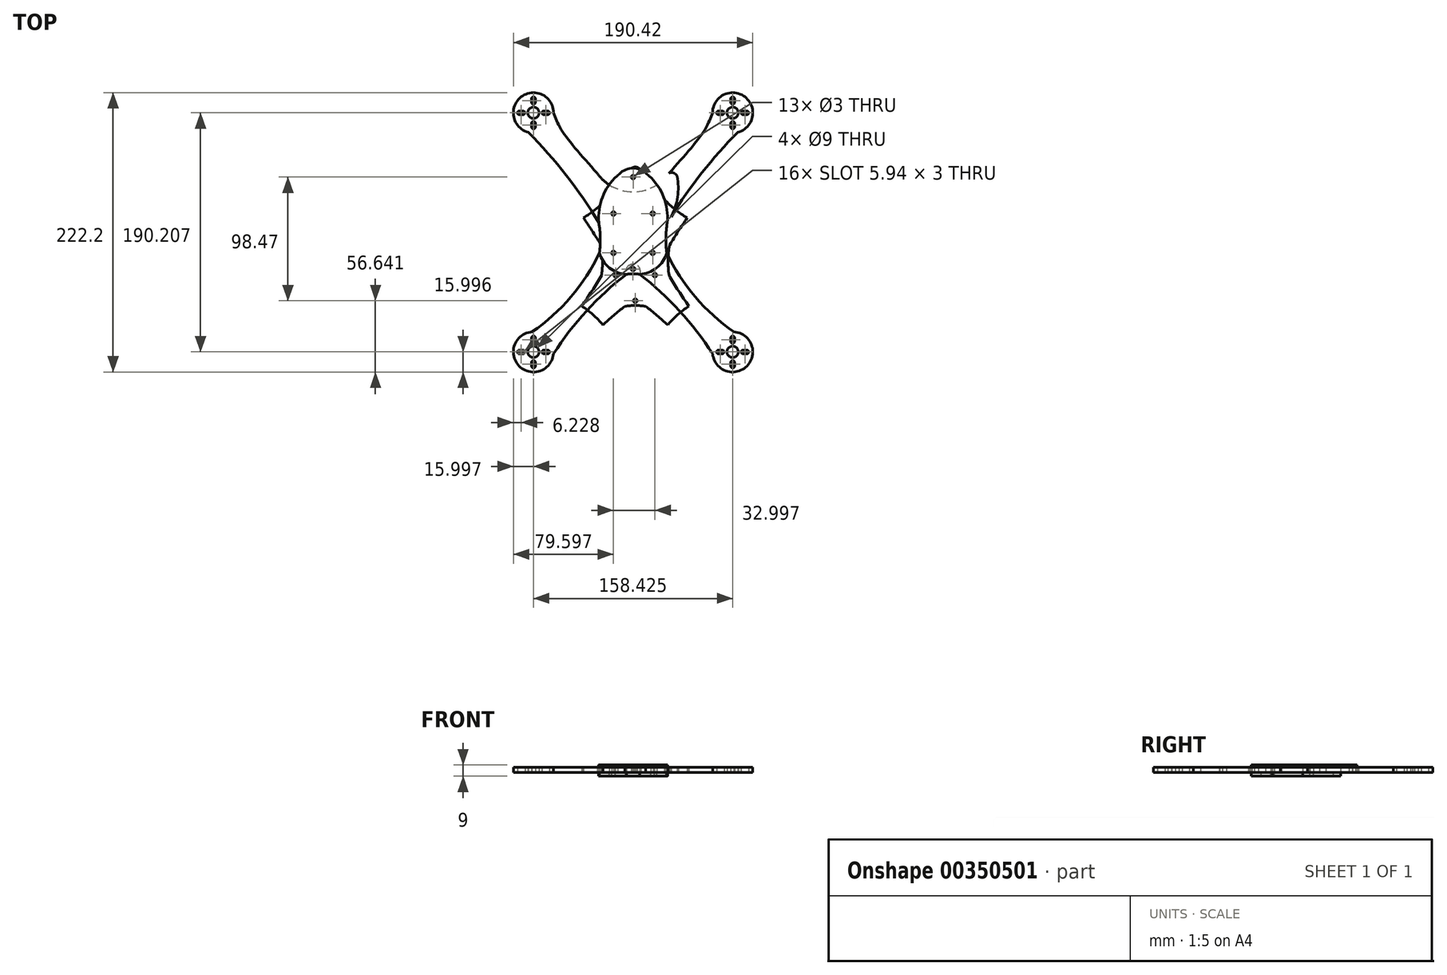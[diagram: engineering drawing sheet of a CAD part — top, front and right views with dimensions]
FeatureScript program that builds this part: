
annotation { "Feature Type Name" : "Feature", "Feature Type Description" : "" }
export const myFeature = defineFeature(function(context is Context, id is Id, definition is map)
    precondition{}
    {
        {
            var Q0;
            Q0=qCreatedBy(makeId("Top.planeOp"),FACE);
            var sketch = newSketch(context, id + "F0", { "sketchPlane" : qUnion([Q0])});
            skArc(sketch, "E0", {"start": v(-12.34, -15.33) * mm, "mid": v(-13.84, -13.83) * mm, "end": v(-15.34, -15.33) * mm});
            skArc(sketch, "E1.MirrorC", {"start": v(15.88, -15.33) * mm, "mid": v(17.38, -13.83) * mm, "end": v(18.88, -15.33) * mm});
            skArc(sketch, "E2.MirrorC", {"start": v(-12.34, 15.9) * mm, "mid": v(-13.84, 17.4) * mm, "end": v(-15.34, 15.9) * mm});
            skCircle(sketch, "E3.MirrorC", {"center": v(17.38, 15.9) * mm, "radius": 1.5 * mm});
            skPoint(sketch, "E4.orphan", {"position": v(-15.34, -15.33) * mm});
            skPoint(sketch, "E5.orphan", {"position": v(-15.34, -46.55) * mm});
            skPoint(sketch, "E6.orphan", {"position": v(-12.34, -46.55) * mm});
            skPoint(sketch, "E7.orphan", {"position": v(18.88, -46.55) * mm});
            skPoint(sketch, "E8.orphan", {"position": v(15.88, -46.55) * mm});
            skPoint(sketch, "E9.orphan", {"position": v(18.88, -15.33) * mm});
            skLineSegment(sketch, "E10.trimOffspring", {"start": v(-15.34, -16.96) * mm, "end": v(-15.48, -16.96) * mm});
            skPoint(sketch, "E11.trimOffspring.end.orphan", {"position": v(-12.34, -15.33) * mm});
            skCircle(sketch, "E12", {"center": v(1.77, 64.96) * mm, "radius": 1.5 * mm});
            skPoint(sketch, "E12.centerSnap0", {"position": v(1.77, 20) * mm});
            skCircle(sketch, "E13", {"center": v(1.77, -35.77) * mm, "radius": 1.5 * mm});
            skPoint(sketch, "E14.end.orphan", {"position": v(24.58, 37.35) * mm});
            skPoint(sketch, "E14.start.orphan", {"position": v(20.96, 39.37) * mm});
            skPoint(sketch, "E15.MirrorCS.end.orphan", {"position": v(-21.04, 37.35) * mm});
            skPoint(sketch, "E15.MirrorCS.start.orphan", {"position": v(-17.42, 39.37) * mm});
            skArc(sketch, "E16", {"start": v(15.88, -15.33) * mm, "mid": v(17.38, -16.83) * mm, "end": v(18.88, -15.33) * mm});
            skArc(sketch, "E17", {"start": v(-15.34, -15.33) * mm, "mid": v(-13.84, -16.83) * mm, "end": v(-12.34, -15.33) * mm});
            skArc(sketch, "E18", {"start": v(-15.34, 15.9) * mm, "mid": v(-13.84, 14.4) * mm, "end": v(-12.34, 15.9) * mm});
            skArc(sketch, "E19.MirrorCS", {"start": v(82.48, 107.32) * mm, "mid": v(80.98, 108.82) * mm, "end": v(79.48, 107.32) * mm});
            skLineSegment(sketch, "E20.MirrorCS", {"start": v(82.48, 104.38) * mm, "end": v(82.48, 107.32) * mm});
            skArc(sketch, "E21.MirrorCS", {"start": v(79.48, 104.38) * mm, "mid": v(80.98, 102.88) * mm, "end": v(82.48, 104.38) * mm});
            skLineSegment(sketch, "E22.MirrorCS", {"start": v(79.48, 104.38) * mm, "end": v(79.48, 107.32) * mm});
            skArc(sketch, "E23.MirrorCS", {"start": v(72.68, 94.58) * mm, "mid": v(74.18, 96.08) * mm, "end": v(72.68, 97.58) * mm});
            skLineSegment(sketch, "E24.MirrorCS", {"start": v(72.68, 97.58) * mm, "end": v(69.74, 97.58) * mm});
            skLineSegment(sketch, "E25.MirrorCS", {"start": v(72.68, 94.58) * mm, "end": v(69.74, 94.58) * mm});
            skArc(sketch, "E26.MirrorCS", {"start": v(69.74, 97.58) * mm, "mid": v(68.24, 96.08) * mm, "end": v(69.74, 94.58) * mm});
            skArc(sketch, "E27.MirrorCS", {"start": v(79.48, 87.78) * mm, "mid": v(80.98, 89.28) * mm, "end": v(82.48, 87.78) * mm});
            skLineSegment(sketch, "E28.MirrorCS", {"start": v(79.48, 87.78) * mm, "end": v(79.48, 84.84) * mm});
            skLineSegment(sketch, "E29.MirrorCS", {"start": v(82.48, 87.78) * mm, "end": v(82.48, 84.84) * mm});
            skArc(sketch, "E30.MirrorCS", {"start": v(82.48, 84.84) * mm, "mid": v(80.98, 83.34) * mm, "end": v(79.48, 84.84) * mm});
            skLineSegment(sketch, "E31.MirrorCS", {"start": v(87.78, 96.08) * mm, "end": v(87.78, 96.08) * mm});
            skArc(sketch, "E32.MirrorCS", {"start": v(89.28, 94.58) * mm, "mid": v(87.78, 96.08) * mm, "end": v(89.28, 97.58) * mm});
            skLineSegment(sketch, "E33.MirrorCS", {"start": v(89.28, 94.58) * mm, "end": v(92.22, 94.58) * mm});
            skArc(sketch, "E34.MirrorCS", {"start": v(92.22, 97.58) * mm, "mid": v(93.72, 96.08) * mm, "end": v(92.22, 94.58) * mm});
            skLineSegment(sketch, "E35.MirrorCS", {"start": v(89.28, 97.58) * mm, "end": v(92.22, 97.58) * mm});
            skLineSegment(sketch, "E36.MirrorCS", {"start": v(-84.24, 96.08) * mm, "end": v(-84.24, 96.08) * mm});
            skLineSegment(sketch, "E37.MirrorCS", {"start": v(-78.94, 87.78) * mm, "end": v(-78.94, 84.84) * mm});
            skLineSegment(sketch, "E38.MirrorCS", {"start": v(-85.74, 97.58) * mm, "end": v(-88.68, 97.58) * mm});
            skLineSegment(sketch, "E39.MirrorCS", {"start": v(-78.94, 104.38) * mm, "end": v(-78.94, 107.32) * mm});
            skLineSegment(sketch, "E40.MirrorCS", {"start": v(-75.94, 87.78) * mm, "end": v(-75.94, 84.84) * mm});
            skLineSegment(sketch, "E41.MirrorCS", {"start": v(-69.14, 97.58) * mm, "end": v(-66.2, 97.58) * mm});
            skArc(sketch, "E42.MirrorCS", {"start": v(-75.94, 87.78) * mm, "mid": v(-77.44, 89.28) * mm, "end": v(-78.94, 87.78) * mm});
            skLineSegment(sketch, "E43.MirrorCS", {"start": v(-85.74, 94.58) * mm, "end": v(-88.68, 94.58) * mm});
            skLineSegment(sketch, "E44.MirrorCS", {"start": v(-75.94, 104.38) * mm, "end": v(-75.94, 107.32) * mm});
            skLineSegment(sketch, "E45.MirrorCS", {"start": v(-69.14, 94.58) * mm, "end": v(-66.2, 94.58) * mm});
            skArc(sketch, "E46.MirrorCS", {"start": v(-85.74, 94.58) * mm, "mid": v(-84.24, 96.08) * mm, "end": v(-85.74, 97.58) * mm});
            skArc(sketch, "E47.MirrorCS", {"start": v(-88.68, 97.58) * mm, "mid": v(-90.18, 96.08) * mm, "end": v(-88.68, 94.58) * mm});
            skArc(sketch, "E48.MirrorCS", {"start": v(-78.94, 84.84) * mm, "mid": v(-77.44, 83.34) * mm, "end": v(-75.94, 84.84) * mm});
            skArc(sketch, "E49.MirrorCS", {"start": v(-66.2, 97.58) * mm, "mid": v(-64.7, 96.08) * mm, "end": v(-66.2, 94.58) * mm});
            skArc(sketch, "E50.MirrorCS", {"start": v(-69.14, 94.58) * mm, "mid": v(-70.64, 96.08) * mm, "end": v(-69.14, 97.58) * mm});
            skArc(sketch, "E51.MirrorCS", {"start": v(-75.94, 104.38) * mm, "mid": v(-77.44, 102.88) * mm, "end": v(-78.94, 104.38) * mm});
            skArc(sketch, "E52.MirrorCS", {"start": v(-78.94, 107.32) * mm, "mid": v(-77.44, 108.82) * mm, "end": v(-75.94, 107.32) * mm});
            skArc(sketch, "E53", {"start": v(30.33, 48.04) * mm, "mid": v(49.63, 70.62) * mm, "end": v(64.98, 96.06) * mm});
            skPoint(sketch, "E54.orphan", {"position": v(15.88, -42.75) * mm});
            skArc(sketch, "E55.MirrorCS", {"start": v(-26.79, 48.04) * mm, "mid": v(-46.1, 70.62) * mm, "end": v(-61.44, 96.06) * mm});
            skPoint(sketch, "E56.orphan", {"position": v(-6.2, -43.06) * mm});
            skPoint(sketch, "E57.orphan", {"position": v(9.74, -43.06) * mm});
            skPoint(sketch, "E58.orphan", {"position": v(80.98, 89.28) * mm});
            skPoint(sketch, "E59.trimOffspring.end.orphan", {"position": v(81.18, 96.27) * mm});
            skPoint(sketch, "E60.MirrorCS.start.orphan", {"position": v(84.98, 96.08) * mm});
            skPoint(sketch, "E61.orphan", {"position": v(-77.44, 89.28) * mm});
            skPoint(sketch, "E62.orphan", {"position": v(-77.64, 96.27) * mm});
            skPoint(sketch, "E63.MirrorCS.start.orphan", {"position": v(-77.44, 92.08) * mm});
            skPoint(sketch, "E64.MirrorCS.start.orphan", {"position": v(-6.54, -40.11) * mm});
            skPoint(sketch, "E65.orphan", {"position": v(-6.78, -48.4) * mm});
            skPoint(sketch, "E66.orphan", {"position": v(10.32, -48.4) * mm});
            skPoint(sketch, "E67.start.orphan", {"position": v(81.18, 0.98) * mm});
            skPoint(sketch, "E68.trimOffspring.end.orphan", {"position": v(1.77, -17.71) * mm});
            skPoint(sketch, "E69.MirrorCS.start.orphan", {"position": v(10.04, -30.06) * mm});
            skPoint(sketch, "E70.orphan", {"position": v(10.04, 34.15) * mm});
            skPoint(sketch, "E71.0.internal.orphan", {"position": v(1.77, 60.1) * mm});
            skPoint(sketch, "E71.3.internal.orphan", {"position": v(1.77, 47.68) * mm});
            skPoint(sketch, "E72.orphan", {"position": v(-15.48, 17.54) * mm});
            skPoint(sketch, "E73.orphan", {"position": v(1.77, 18.29) * mm});
            skPoint(sketch, "E74.orphan", {"position": v(19.77, 18.29) * mm});
            skPoint(sketch, "E75.top.start.orphan", {"position": v(19.02, 17.54) * mm});
            skPoint(sketch, "E76.MirrorCS.end.orphan", {"position": v(19.77, -17.71) * mm});
            skPoint(sketch, "E77.MirrorCS.1.internal.orphan", {"position": v(1.77, -50.77) * mm});
            skArc(sketch, "E78", {"start": v(16.09, 50.44) * mm, "mid": v(22.8, 46.88) * mm, "end": v(30.33, 48.04) * mm});
            skFitSpline(sketch, "E79", {"points": [v(16.09, 50.44) * mm, v(11.26, 61.8) * mm, v(7, 67.55) * mm, v(4.1, 70.13) * mm, v(2.12, 70.7) * mm], "startDerivative": vector(-12.46, 33.65) * mm, "endDerivative": vector(-13.1, 2.1) * mm});
            skFitSpline(sketch, "E80.MirrorCS", {"points": [v(-12.5, 50.44) * mm, v(-3.42, 67.55) * mm, v(-0.5, 70.13) * mm, v(1.47, 70.7) * mm], "startDerivative": vector(12.46, 33.65) * mm, "endDerivative": vector(13.1, 2.1) * mm});
            skLineSegment(sketch, "E81", {"start": v(1.47, 70.7) * mm, "end": v(2.12, 70.7) * mm});
            skLineSegment(sketch, "E82", {"start": v(1.42, 70.7) * mm, "end": v(2.12, 70.7) * mm});
            skCircle(sketch, "E83", {"center": v(80.98, 96.08) * mm, "radius": 4.5 * mm});
            skCircle(sketch, "E84.MirrorC", {"center": v(-77.44, 96.08) * mm, "radius": 4.5 * mm});
            skArc(sketch, "E85", {"start": v(10.08, -40.11) * mm, "mid": v(1.77, -39.52) * mm, "end": v(-6.54, -40.11) * mm});
            skArc(sketch, "E86", {"start": v(-25.48, 8.63) * mm, "mid": v(-51.36, 46.26) * mm, "end": v(-81.48, 80.6) * mm});
            skArc(sketch, "E87.MirrorCS", {"start": v(29.02, 8.63) * mm, "mid": v(54.9, 46.26) * mm, "end": v(85.02, 80.6) * mm});
            skArc(sketch, "E88", {"start": v(-25.05, -15.37) * mm, "mid": v(-24.3, -3.35) * mm, "end": v(-25.48, 8.63) * mm});
            skArc(sketch, "E89.MirrorCS", {"start": v(28.6, -15.37) * mm, "mid": v(27.85, -3.35) * mm, "end": v(29.02, 8.63) * mm});
            skArc(sketch, "E90", {"start": v(-61.44, 96.06) * mm, "mid": v(-87.22, 108.75) * mm, "end": v(-81.48, 80.6) * mm});
            skArc(sketch, "E91.MirrorCS", {"start": v(64.98, 96.06) * mm, "mid": v(90.76, 108.75) * mm, "end": v(85.02, 80.6) * mm});
            skCircle(sketch, "E92", {"center": v(1.77, 64.96) * mm, "radius": 4.52 * mm});
            skArc(sketch, "E93.MirrorCS", {"start": v(-12.5, 50.44) * mm, "mid": v(-19.22, 46.88) * mm, "end": v(-26.74, 48.04) * mm});
            skFitSpline(sketch, "E94.MirrorCS", {"points": [v(-12.5, 50.44) * mm, v(-7.67, 61.8) * mm, v(-3.42, 67.55) * mm, v(-0.5, 70.13) * mm, v(1.47, 70.7) * mm], "startDerivative": vector(12.46, 33.65) * mm, "endDerivative": vector(13.1, 2.1) * mm});
            skLineSegment(sketch, "E95.MirrorCS", {"start": v(-89.55, -103.58) * mm, "end": v(-89.55, -103.58) * mm});
            skLineSegment(sketch, "E96.MirrorCS", {"start": v(-91.05, -105.08) * mm, "end": v(-94, -105.08) * mm});
            skLineSegment(sketch, "E97.MirrorCS", {"start": v(-84.25, -111.88) * mm, "end": v(-84.25, -114.83) * mm});
            skLineSegment(sketch, "E98.MirrorCS", {"start": v(-81.25, -95.29) * mm, "end": v(-81.25, -92.34) * mm});
            skLineSegment(sketch, "E99.MirrorCS", {"start": v(-91.05, -102.08) * mm, "end": v(-94, -102.08) * mm});
            skLineSegment(sketch, "E100.MirrorCS", {"start": v(-74.45, -105.08) * mm, "end": v(-71.5, -105.08) * mm});
            skLineSegment(sketch, "E101.MirrorCS", {"start": v(-74.45, -102.08) * mm, "end": v(-71.5, -102.08) * mm});
            skArc(sketch, "E102.MirrorCS", {"start": v(-91.05, -102.08) * mm, "mid": v(-89.55, -103.58) * mm, "end": v(-91.05, -105.08) * mm});
            skArc(sketch, "E103.MirrorCS", {"start": v(-81.25, -95.29) * mm, "mid": v(-82.75, -96.79) * mm, "end": v(-84.25, -95.29) * mm});
            skLineSegment(sketch, "E104.MirrorCS", {"start": v(-84.25, -95.29) * mm, "end": v(-84.25, -92.34) * mm});
            skLineSegment(sketch, "E105.MirrorCS", {"start": v(-81.25, -111.88) * mm, "end": v(-81.25, -114.83) * mm});
            skArc(sketch, "E106.MirrorCS", {"start": v(-94, -105.08) * mm, "mid": v(-95.5, -103.58) * mm, "end": v(-94, -102.08) * mm});
            skCircle(sketch, "E107.MirrorC", {"center": v(-82.75, -103.58) * mm, "radius": 4.5 * mm});
            skArc(sketch, "E108.MirrorCS", {"start": v(-84.25, -114.83) * mm, "mid": v(-82.75, -116.33) * mm, "end": v(-81.25, -114.83) * mm});
            skArc(sketch, "E109.MirrorCS", {"start": v(-71.5, -105.08) * mm, "mid": v(-70, -103.58) * mm, "end": v(-71.5, -102.08) * mm});
            skArc(sketch, "E110.MirrorCS", {"start": v(-84.25, -92.34) * mm, "mid": v(-82.75, -90.84) * mm, "end": v(-81.25, -92.34) * mm});
            skArc(sketch, "E111.MirrorCS", {"start": v(-81.25, -111.88) * mm, "mid": v(-82.75, -110.38) * mm, "end": v(-84.25, -111.88) * mm});
            skArc(sketch, "E112.MirrorCS", {"start": v(-74.45, -102.08) * mm, "mid": v(-75.95, -103.58) * mm, "end": v(-74.45, -105.08) * mm});
            skArc(sketch, "E113", {"start": v(-83.86, -87.62) * mm, "mid": v(-94.16, -114.8) * mm, "end": v(-66.81, -104.96) * mm});
            skCircle(sketch, "E114", {"center": v(-77.44, -94.13) * mm, "radius": 63.5 * mm});
            skCircle(sketch, "E115", {"center": v(-82.75, -103.58) * mm, "radius": 76.2 * mm});
            skCircle(sketch, "E116.MirrorC", {"center": v(86.34, -103.58) * mm, "radius": 76.2 * mm});
            skLineSegment(sketch, "E117.MirrorCS", {"start": v(93.14, -103.58) * mm, "end": v(93.14, -103.58) * mm});
            skLineSegment(sketch, "E118.MirrorCS", {"start": v(78.04, -105.08) * mm, "end": v(75.1, -105.08) * mm});
            skLineSegment(sketch, "E119.MirrorCS", {"start": v(84.84, -95.29) * mm, "end": v(84.84, -92.34) * mm});
            skArc(sketch, "E120.MirrorCS", {"start": v(94.64, -102.08) * mm, "mid": v(93.14, -103.58) * mm, "end": v(94.64, -105.08) * mm});
            skLineSegment(sketch, "E121.MirrorCS", {"start": v(87.84, -95.29) * mm, "end": v(87.84, -92.34) * mm});
            skLineSegment(sketch, "E122.MirrorCS", {"start": v(94.64, -102.08) * mm, "end": v(97.58, -102.08) * mm});
            skLineSegment(sketch, "E123.MirrorCS", {"start": v(84.84, -111.88) * mm, "end": v(84.84, -114.83) * mm});
            skArc(sketch, "E124.MirrorCS", {"start": v(84.84, -111.88) * mm, "mid": v(86.34, -110.38) * mm, "end": v(87.84, -111.88) * mm});
            skLineSegment(sketch, "E125.MirrorCS", {"start": v(87.84, -111.88) * mm, "end": v(87.84, -114.83) * mm});
            skLineSegment(sketch, "E126.MirrorCS", {"start": v(94.64, -105.08) * mm, "end": v(97.58, -105.08) * mm});
            skLineSegment(sketch, "E127.MirrorCS", {"start": v(78.04, -102.08) * mm, "end": v(75.1, -102.08) * mm});
            skArc(sketch, "E128.MirrorCS", {"start": v(78.04, -102.08) * mm, "mid": v(79.54, -103.58) * mm, "end": v(78.04, -105.08) * mm});
            skArc(sketch, "E129.MirrorCS", {"start": v(75.1, -105.08) * mm, "mid": v(73.6, -103.58) * mm, "end": v(75.1, -102.08) * mm});
            skArc(sketch, "E130.MirrorCS", {"start": v(84.84, -95.29) * mm, "mid": v(86.34, -96.79) * mm, "end": v(87.84, -95.29) * mm});
            skArc(sketch, "E131.MirrorCS", {"start": v(87.84, -114.83) * mm, "mid": v(86.34, -116.33) * mm, "end": v(84.84, -114.83) * mm});
            skArc(sketch, "E132.MirrorCS", {"start": v(87.45, -87.62) * mm, "mid": v(97.75, -114.8) * mm, "end": v(70.4, -104.96) * mm});
            skArc(sketch, "E133.MirrorCS", {"start": v(97.58, -105.08) * mm, "mid": v(99.08, -103.58) * mm, "end": v(97.58, -102.08) * mm});
            skCircle(sketch, "E134.MirrorC", {"center": v(86.34, -103.58) * mm, "radius": 4.5 * mm});
            skArc(sketch, "E135.MirrorCS", {"start": v(87.84, -92.34) * mm, "mid": v(86.34, -90.84) * mm, "end": v(84.84, -92.34) * mm});
            skCircle(sketch, "E136", {"center": v(-77.64, 96.27) * mm, "radius": 76.2 * mm});
            skCircle(sketch, "E137.MirrorC", {"center": v(81.18, 96.27) * mm, "radius": 76.2 * mm});
            skArc(sketch, "E138", {"start": v(-6.54, -40.11) * mm, "mid": v(-39.3, -70.1) * mm, "end": v(-66.81, -104.96) * mm});
            skArc(sketch, "E139", {"start": v(-83.86, -87.62) * mm, "mid": v(-51.54, -53.88) * mm, "end": v(-25.05, -15.37) * mm});
            skArc(sketch, "E140.MirrorCS", {"start": v(10.08, -40.11) * mm, "mid": v(42.85, -70.1) * mm, "end": v(70.35, -104.96) * mm});
            skArc(sketch, "E141.MirrorCS", {"start": v(87.4, -87.62) * mm, "mid": v(55.08, -53.88) * mm, "end": v(28.6, -15.37) * mm});
            skSolve(sketch);
        }
        {
            var Q0;
            Q0=makeQuery(id+"F0.imprint","IMPRINT",FACE,{"disambiguationData":[TD([[makeQuery(id+"F0.imprint","IMPRINT",EDGE,{"derivedFrom":sQuery(id+"F0.wireOp",EDGE,"E0")}),-1.0]])]});
            extrude(context, id + "F1", {"entities" : qUnion([Q0]), "depth" : 4 * mm});
        }
        {
            var Q0;
            Q0=qCreatedBy(makeId("Top.planeOp"),FACE);
            var sketch = newSketch(context, id + "F2", { "sketchPlane" : qUnion([Q0])});
            skArc(sketch, "E142", {"start": v(-14.11, 2.39) * mm, "mid": v(-15.61, 3.89) * mm, "end": v(-17.11, 2.39) * mm});
            skArc(sketch, "E143.MirrorC", {"start": v(14.11, 2.39) * mm, "mid": v(15.61, 3.89) * mm, "end": v(17.11, 2.39) * mm});
            skArc(sketch, "E144.MirrorC", {"start": v(-14.11, 33.61) * mm, "mid": v(-15.61, 35.11) * mm, "end": v(-17.11, 33.61) * mm});
            skCircle(sketch, "E145.MirrorC", {"center": v(15.61, 33.61) * mm, "radius": 1.5 * mm});
            skPoint(sketch, "E146.orphan", {"position": v(-17.11, 2.39) * mm});
            skPoint(sketch, "E147.orphan", {"position": v(-17.11, -28.84) * mm});
            skPoint(sketch, "E148.orphan", {"position": v(-14.11, -28.84) * mm});
            skPoint(sketch, "E149.orphan", {"position": v(17.11, -28.84) * mm});
            skPoint(sketch, "E150.orphan", {"position": v(14.11, -28.84) * mm});
            skPoint(sketch, "E151.orphan", {"position": v(17.11, 2.39) * mm});
            skLineSegment(sketch, "E152.trimOffspring", {"start": v(-17.11, 0.75) * mm, "end": v(-17.25, 0.75) * mm});
            skPoint(sketch, "E153.trimOffspring.end.orphan", {"position": v(-14.11, 2.39) * mm});
            skCircle(sketch, "E154", {"center": v(0.03, 62.7) * mm, "radius": 1.5 * mm});
            skPoint(sketch, "E154.centerSnap0", {"position": v(0.03, 37.72) * mm});
            skCircle(sketch, "E155", {"center": v(0, -10.49) * mm, "radius": 1.5 * mm});
            skPoint(sketch, "E156.end.orphan", {"position": v(22.8, 55.07) * mm});
            skPoint(sketch, "E156.start.orphan", {"position": v(19.19, 57.09) * mm});
            skPoint(sketch, "E157.MirrorCS.end.orphan", {"position": v(-22.8, 55.07) * mm});
            skPoint(sketch, "E157.MirrorCS.start.orphan", {"position": v(-19.19, 57.09) * mm});
            skArc(sketch, "E158", {"start": v(14.11, 2.39) * mm, "mid": v(15.61, 0.89) * mm, "end": v(17.11, 2.39) * mm});
            skArc(sketch, "E159", {"start": v(-17.11, 2.39) * mm, "mid": v(-15.61, 0.89) * mm, "end": v(-14.11, 2.39) * mm});
            skArc(sketch, "E160", {"start": v(-17.11, 33.61) * mm, "mid": v(-15.61, 32.11) * mm, "end": v(-14.11, 33.61) * mm});
            skCircle(sketch, "E161", {"center": v(79.21, 113.8) * mm, "radius": 4.5 * mm});
            skArc(sketch, "E162.MirrorCS", {"start": v(80.71, 125.03) * mm, "mid": v(79.21, 126.53) * mm, "end": v(77.71, 125.03) * mm});
            skLineSegment(sketch, "E163.MirrorCS", {"start": v(80.71, 122.1) * mm, "end": v(80.71, 125.03) * mm});
            skArc(sketch, "E164.MirrorCS", {"start": v(77.71, 122.1) * mm, "mid": v(79.21, 120.6) * mm, "end": v(80.71, 122.1) * mm});
            skLineSegment(sketch, "E165.MirrorCS", {"start": v(77.71, 122.1) * mm, "end": v(77.71, 125.03) * mm});
            skArc(sketch, "E166.MirrorCS", {"start": v(70.91, 112.3) * mm, "mid": v(72.41, 113.8) * mm, "end": v(70.91, 115.3) * mm});
            skLineSegment(sketch, "E167.MirrorCS", {"start": v(70.91, 115.3) * mm, "end": v(67.97, 115.3) * mm});
            skLineSegment(sketch, "E168.MirrorCS", {"start": v(70.91, 112.3) * mm, "end": v(67.97, 112.3) * mm});
            skArc(sketch, "E169.MirrorCS", {"start": v(67.97, 115.3) * mm, "mid": v(66.47, 113.8) * mm, "end": v(67.97, 112.3) * mm});
            skArc(sketch, "E170.MirrorCS", {"start": v(77.71, 105.5) * mm, "mid": v(79.21, 107) * mm, "end": v(80.71, 105.5) * mm});
            skLineSegment(sketch, "E171.MirrorCS", {"start": v(77.71, 105.5) * mm, "end": v(77.71, 102.55) * mm});
            skLineSegment(sketch, "E172.MirrorCS", {"start": v(80.71, 105.5) * mm, "end": v(80.71, 102.55) * mm});
            skArc(sketch, "E173.MirrorCS", {"start": v(80.71, 102.55) * mm, "mid": v(79.21, 101.05) * mm, "end": v(77.71, 102.55) * mm});
            skLineSegment(sketch, "E174.MirrorCS", {"start": v(86.01, 113.8) * mm, "end": v(86.01, 113.8) * mm});
            skArc(sketch, "E175.MirrorCS", {"start": v(87.51, 112.3) * mm, "mid": v(86.01, 113.8) * mm, "end": v(87.51, 115.3) * mm});
            skLineSegment(sketch, "E176.MirrorCS", {"start": v(87.51, 112.3) * mm, "end": v(90.45, 112.3) * mm});
            skArc(sketch, "E177.MirrorCS", {"start": v(90.45, 115.3) * mm, "mid": v(91.95, 113.8) * mm, "end": v(90.45, 112.3) * mm});
            skLineSegment(sketch, "E178.MirrorCS", {"start": v(87.51, 115.3) * mm, "end": v(90.45, 115.3) * mm});
            skLineSegment(sketch, "E179.MirrorCS", {"start": v(-86.01, 113.8) * mm, "end": v(-86.01, 113.8) * mm});
            skLineSegment(sketch, "E180.MirrorCS", {"start": v(-80.71, 105.5) * mm, "end": v(-80.71, 102.55) * mm});
            skLineSegment(sketch, "E181.MirrorCS", {"start": v(-87.51, 115.3) * mm, "end": v(-90.45, 115.3) * mm});
            skLineSegment(sketch, "E182.MirrorCS", {"start": v(-80.71, 122.1) * mm, "end": v(-80.71, 125.03) * mm});
            skLineSegment(sketch, "E183.MirrorCS", {"start": v(-77.71, 105.5) * mm, "end": v(-77.71, 102.55) * mm});
            skLineSegment(sketch, "E184.MirrorCS", {"start": v(-70.91, 115.3) * mm, "end": v(-67.97, 115.3) * mm});
            skArc(sketch, "E185.MirrorCS", {"start": v(-77.71, 105.5) * mm, "mid": v(-79.21, 107) * mm, "end": v(-80.71, 105.5) * mm});
            skLineSegment(sketch, "E186.MirrorCS", {"start": v(-87.51, 112.3) * mm, "end": v(-90.45, 112.3) * mm});
            skLineSegment(sketch, "E187.MirrorCS", {"start": v(-77.71, 122.1) * mm, "end": v(-77.71, 125.03) * mm});
            skLineSegment(sketch, "E188.MirrorCS", {"start": v(-70.91, 112.3) * mm, "end": v(-67.97, 112.3) * mm});
            skArc(sketch, "E189.MirrorCS", {"start": v(-87.51, 112.3) * mm, "mid": v(-86.01, 113.8) * mm, "end": v(-87.51, 115.3) * mm});
            skLineSegment(sketch, "E190.MirrorCS", {"start": v(86.01, -76.41) * mm, "end": v(86.01, -76.41) * mm});
            skLineSegment(sketch, "E191.MirrorCS", {"start": v(70.91, -77.91) * mm, "end": v(67.97, -77.91) * mm});
            skArc(sketch, "E192.MirrorCS", {"start": v(77.71, -68.11) * mm, "mid": v(79.21, -69.61) * mm, "end": v(80.71, -68.11) * mm});
            skLineSegment(sketch, "E193.MirrorCS", {"start": v(77.71, -68.11) * mm, "end": v(77.71, -65.17) * mm});
            skLineSegment(sketch, "E194.MirrorCS", {"start": v(70.91, -74.91) * mm, "end": v(67.97, -74.91) * mm});
            skLineSegment(sketch, "E195.MirrorCS", {"start": v(80.71, -84.71) * mm, "end": v(80.71, -87.65) * mm});
            skLineSegment(sketch, "E196.MirrorCS", {"start": v(77.71, -84.71) * mm, "end": v(77.71, -87.65) * mm});
            skLineSegment(sketch, "E197.MirrorCS", {"start": v(80.71, -68.11) * mm, "end": v(80.71, -65.17) * mm});
            skArc(sketch, "E198.MirrorCS", {"start": v(87.51, -74.91) * mm, "mid": v(86.01, -76.41) * mm, "end": v(87.51, -77.91) * mm});
            skLineSegment(sketch, "E199.MirrorCS", {"start": v(87.51, -74.91) * mm, "end": v(90.45, -74.91) * mm});
            skLineSegment(sketch, "E200.MirrorCS", {"start": v(87.51, -77.91) * mm, "end": v(90.45, -77.91) * mm});
            skArc(sketch, "E201.MirrorCS", {"start": v(70.91, -74.91) * mm, "mid": v(72.41, -76.41) * mm, "end": v(70.91, -77.91) * mm});
            skArc(sketch, "E202.MirrorCS", {"start": v(80.71, -65.17) * mm, "mid": v(79.21, -63.67) * mm, "end": v(77.71, -65.17) * mm});
            skArc(sketch, "E203.MirrorCS", {"start": v(77.71, -84.71) * mm, "mid": v(79.21, -83.21) * mm, "end": v(80.71, -84.71) * mm});
            skArc(sketch, "E204.MirrorCS", {"start": v(90.45, -77.91) * mm, "mid": v(91.95, -76.41) * mm, "end": v(90.45, -74.91) * mm});
            skArc(sketch, "E205.MirrorCS", {"start": v(67.97, -77.91) * mm, "mid": v(66.47, -76.41) * mm, "end": v(67.97, -74.91) * mm});
            skCircle(sketch, "E206.MirrorC", {"center": v(79.21, -76.41) * mm, "radius": 4.5 * mm});
            skArc(sketch, "E207.MirrorCS", {"start": v(80.71, -87.65) * mm, "mid": v(79.21, -89.15) * mm, "end": v(77.71, -87.65) * mm});
            skLineSegment(sketch, "E208.MirrorCS", {"start": v(-86.01, -76.41) * mm, "end": v(-86.01, -76.41) * mm});
            skLineSegment(sketch, "E209.MirrorCS", {"start": v(-87.51, -77.91) * mm, "end": v(-90.45, -77.91) * mm});
            skLineSegment(sketch, "E210.MirrorCS", {"start": v(-80.71, -84.71) * mm, "end": v(-80.71, -87.65) * mm});
            skLineSegment(sketch, "E211.MirrorCS", {"start": v(-77.71, -68.11) * mm, "end": v(-77.71, -65.17) * mm});
            skLineSegment(sketch, "E212.MirrorCS", {"start": v(-87.51, -74.91) * mm, "end": v(-90.45, -74.91) * mm});
            skLineSegment(sketch, "E213.MirrorCS", {"start": v(-70.91, -77.91) * mm, "end": v(-67.97, -77.91) * mm});
            skLineSegment(sketch, "E214.MirrorCS", {"start": v(-70.91, -74.91) * mm, "end": v(-67.97, -74.91) * mm});
            skArc(sketch, "E215.MirrorCS", {"start": v(-87.51, -74.91) * mm, "mid": v(-86.01, -76.41) * mm, "end": v(-87.51, -77.91) * mm});
            skArc(sketch, "E216.MirrorCS", {"start": v(-77.71, -68.11) * mm, "mid": v(-79.21, -69.61) * mm, "end": v(-80.71, -68.11) * mm});
            skLineSegment(sketch, "E217.MirrorCS", {"start": v(-80.71, -68.11) * mm, "end": v(-80.71, -65.17) * mm});
            skLineSegment(sketch, "E218.MirrorCS", {"start": v(-77.71, -84.71) * mm, "end": v(-77.71, -87.65) * mm});
            skArc(sketch, "E219.MirrorCS", {"start": v(-90.45, -77.91) * mm, "mid": v(-91.95, -76.41) * mm, "end": v(-90.45, -74.91) * mm});
            skCircle(sketch, "E220.MirrorC", {"center": v(-79.21, -76.41) * mm, "radius": 4.5 * mm});
            skArc(sketch, "E221.MirrorCS", {"start": v(-80.71, -87.65) * mm, "mid": v(-79.21, -89.15) * mm, "end": v(-77.71, -87.65) * mm});
            skArc(sketch, "E222.MirrorCS", {"start": v(-67.97, -77.91) * mm, "mid": v(-66.47, -76.41) * mm, "end": v(-67.97, -74.91) * mm});
            skArc(sketch, "E223.MirrorCS", {"start": v(-80.71, -65.17) * mm, "mid": v(-79.21, -63.67) * mm, "end": v(-77.71, -65.17) * mm});
            skArc(sketch, "E224.MirrorCS", {"start": v(-77.71, -84.71) * mm, "mid": v(-79.21, -83.21) * mm, "end": v(-80.71, -84.71) * mm});
            skArc(sketch, "E225.MirrorCS", {"start": v(-70.91, -74.91) * mm, "mid": v(-72.41, -76.41) * mm, "end": v(-70.91, -77.91) * mm});
            skCircle(sketch, "E226.MirrorC", {"center": v(-79.21, 113.8) * mm, "radius": 4.5 * mm});
            skArc(sketch, "E227.MirrorCS", {"start": v(-90.45, 115.3) * mm, "mid": v(-91.95, 113.8) * mm, "end": v(-90.45, 112.3) * mm});
            skArc(sketch, "E228.MirrorCS", {"start": v(-80.71, 102.55) * mm, "mid": v(-79.21, 101.05) * mm, "end": v(-77.71, 102.55) * mm});
            skArc(sketch, "E229.MirrorCS", {"start": v(-67.97, 115.3) * mm, "mid": v(-66.47, 113.8) * mm, "end": v(-67.97, 112.3) * mm});
            skArc(sketch, "E230.MirrorCS", {"start": v(-70.91, 112.3) * mm, "mid": v(-72.41, 113.8) * mm, "end": v(-70.91, 115.3) * mm});
            skArc(sketch, "E231.MirrorCS", {"start": v(-77.71, 122.1) * mm, "mid": v(-79.21, 120.6) * mm, "end": v(-80.71, 122.1) * mm});
            skArc(sketch, "E232.MirrorCS", {"start": v(-80.71, 125.03) * mm, "mid": v(-79.21, 126.53) * mm, "end": v(-77.71, 125.03) * mm});
            skArc(sketch, "E233", {"start": v(26.82, 2.34) * mm, "mid": v(49.43, -32.58) * mm, "end": v(80.33, -60.45) * mm});
            skPoint(sketch, "E234.orphan", {"position": v(14.11, -25.03) * mm});
            skArc(sketch, "E235.MirrorCS", {"start": v(-26.82, 2.34) * mm, "mid": v(-49.43, -32.58) * mm, "end": v(-80.33, -60.45) * mm});
            skPoint(sketch, "E236.orphan", {"position": v(-7.97, -25.35) * mm});
            skPoint(sketch, "E237.orphan", {"position": v(7.97, -25.35) * mm});
            skPoint(sketch, "E238.orphan", {"position": v(79.21, 107) * mm});
            skPoint(sketch, "E239.trimOffspring.end.orphan", {"position": v(79.41, 113.98) * mm});
            skPoint(sketch, "E240.MirrorCS.start.orphan", {"position": v(83.21, 113.8) * mm});
            skPoint(sketch, "E241.orphan", {"position": v(-79.21, 107) * mm});
            skPoint(sketch, "E242.orphan", {"position": v(-79.41, 113.98) * mm});
            skPoint(sketch, "E243.MirrorCS.start.orphan", {"position": v(-79.21, 109.8) * mm});
            skPoint(sketch, "E244.orphan", {"position": v(79.41, -76.6) * mm});
            skPoint(sketch, "E245.orphan", {"position": v(79.21, -69.61) * mm});
            skPoint(sketch, "E246.MirrorCS.start.orphan", {"position": v(83.21, -76.41) * mm});
            skPoint(sketch, "E247.orphan", {"position": v(-79.41, -76.6) * mm});
            skPoint(sketch, "E248.orphan", {"position": v(-79.21, -69.61) * mm});
            skPoint(sketch, "E249.MirrorCS.start.orphan", {"position": v(-83.21, -76.41) * mm});
            skPoint(sketch, "E250.MirrorCS.start.orphan", {"position": v(-8.31, -22.4) * mm});
            skPoint(sketch, "E251.orphan", {"position": v(-8.55, -30.69) * mm});
            skPoint(sketch, "E252.orphan", {"position": v(8.55, -30.69) * mm});
            skPoint(sketch, "E253.start.orphan", {"position": v(79.41, 18.69) * mm});
            skPoint(sketch, "E254.trimOffspring.end.orphan", {"position": v(0, 0) * mm});
            skPoint(sketch, "E255.MirrorCS.start.orphan", {"position": v(8.27, -12.35) * mm});
            skPoint(sketch, "E256.orphan", {"position": v(8.27, 51.86) * mm});
            skPoint(sketch, "E257.0.internal.orphan", {"position": v(0, 77.81) * mm});
            skPoint(sketch, "E257.3.internal.orphan", {"position": v(0, 65.4) * mm});
            skPoint(sketch, "E258.orphan", {"position": v(-17.25, 35.25) * mm});
            skPoint(sketch, "E259.orphan", {"position": v(0, 36) * mm});
            skPoint(sketch, "E260.orphan", {"position": v(18, 36) * mm});
            skPoint(sketch, "E261.top.start.orphan", {"position": v(17.25, 35.25) * mm});
            skPoint(sketch, "E262.MirrorCS.end.orphan", {"position": v(18, 0) * mm});
            skPoint(sketch, "E263.MirrorCS.1.internal.orphan", {"position": v(0, -33.05) * mm});
            skArc(sketch, "E264.MirrorCS", {"start": v(5.37, -14.7) * mm, "mid": v(36.96, -43.82) * mm, "end": v(63.27, -77.8) * mm});
            skArc(sketch, "E265", {"start": v(-27.25, 26.35) * mm, "mid": v(-53.13, 63.98) * mm, "end": v(-83.25, 98.31) * mm});
            skArc(sketch, "E266.MirrorCS", {"start": v(27.25, 26.35) * mm, "mid": v(53.13, 63.98) * mm, "end": v(83.25, 98.31) * mm});
            skArc(sketch, "E267", {"start": v(-26.82, 2.34) * mm, "mid": v(-26.08, 14.36) * mm, "end": v(-27.25, 26.35) * mm});
            skArc(sketch, "E268.MirrorCS", {"start": v(26.82, 2.34) * mm, "mid": v(26.08, 14.36) * mm, "end": v(27.25, 26.35) * mm});
            skArc(sketch, "E269", {"start": v(-63.21, 113.77) * mm, "mid": v(-88.99, 126.46) * mm, "end": v(-83.25, 98.31) * mm});
            skArc(sketch, "E270.MirrorCS", {"start": v(63.21, 113.77) * mm, "mid": v(88.99, 126.46) * mm, "end": v(83.25, 98.31) * mm});
            skArc(sketch, "E271", {"start": v(-80.33, -60.45) * mm, "mid": v(-90.62, -87.63) * mm, "end": v(-63.27, -77.8) * mm});
            skArc(sketch, "E272.MirrorCS", {"start": v(80.33, -60.45) * mm, "mid": v(90.62, -87.63) * mm, "end": v(63.27, -77.8) * mm});
            skCircle(sketch, "E273", {"center": v(0.03, 62.7) * mm, "radius": 4.52 * mm});
            skArc(sketch, "E274.MirrorCS", {"start": v(-11.01, 65.14) * mm, "mid": v(-19.9, 61.44) * mm, "end": v(-28.51, 65.75) * mm});
            skArc(sketch, "E275.MirrorCS", {"start": v(11.01, 65.14) * mm, "mid": v(19.9, 61.44) * mm, "end": v(28.51, 65.75) * mm});
            skArc(sketch, "E276", {"start": v(11.01, 65.14) * mm, "mid": v(0, 69.7) * mm, "end": v(-11.01, 65.14) * mm});
            skArc(sketch, "E277.MirrorCS", {"start": v(-5.37, -14.7) * mm, "mid": v(-36.96, -43.82) * mm, "end": v(-63.27, -77.8) * mm});
            skArc(sketch, "E278", {"start": v(5.37, -14.7) * mm, "mid": v(0, -14.33) * mm, "end": v(-5.37, -14.7) * mm});
            skFitSpline(sketch, "E279", {"points": [v(28.51, 65.75) * mm, v(56.44, 99.53) * mm, v(63.21, 113.77) * mm], "startDerivative": vector(53, 59.07) * mm, "endDerivative": vector(13.09, 34.97) * mm});
            skFitSpline(sketch, "E280.MirrorCS", {"points": [v(-28.51, 65.75) * mm, v(-56.44, 99.53) * mm, v(-63.21, 113.77) * mm], "startDerivative": vector(-53, 59.07) * mm, "endDerivative": vector(-13.09, 34.97) * mm});
            skArc(sketch, "E281", {"start": v(-27.25, 26.35) * mm, "mid": v(0, 15.14) * mm, "end": v(27.25, 26.35) * mm});
            skArc(sketch, "E282", {"start": v(26.82, 2.34) * mm, "mid": v(0, 14.78) * mm, "end": v(-26.82, 2.34) * mm});
            skArc(sketch, "E283", {"start": v(-11.01, 65.14) * mm, "mid": v(-23.92, 47.74) * mm, "end": v(-27.25, 26.35) * mm});
            skArc(sketch, "E284", {"start": v(-26.82, 2.34) * mm, "mid": v(-18.75, -9.52) * mm, "end": v(-5.37, -14.7) * mm});
            skArc(sketch, "E285.MirrorCS", {"start": v(11.01, 65.14) * mm, "mid": v(23.92, 47.74) * mm, "end": v(27.25, 26.35) * mm});
            skArc(sketch, "E286.MirrorCS", {"start": v(26.82, 2.34) * mm, "mid": v(18.75, -9.52) * mm, "end": v(5.37, -14.7) * mm});
            skArc(sketch, "E287", {"start": v(-28.51, 65.75) * mm, "mid": v(0, 50.89) * mm, "end": v(28.51, 65.75) * mm});
            skArc(sketch, "E288", {"start": v(-28.51, 65.75) * mm, "mid": v(-32.27, 65.94) * mm, "end": v(-35.01, 63.37) * mm});
            skArc(sketch, "E289", {"start": v(-35.01, 63.37) * mm, "mid": v(-34.92, 44.06) * mm, "end": v(-27.25, 26.35) * mm});
            skArc(sketch, "E290.MirrorCS", {"start": v(28.51, 65.75) * mm, "mid": v(32.27, 65.94) * mm, "end": v(35.01, 63.37) * mm});
            skArc(sketch, "E291.MirrorCS", {"start": v(35.01, 63.37) * mm, "mid": v(34.92, 44.06) * mm, "end": v(27.25, 26.35) * mm});
            skArc(sketch, "E292", {"start": v(5.37, -14.7) * mm, "mid": v(0, -6.64) * mm, "end": v(-5.37, -14.7) * mm});
            skSolve(sketch);
        }
        {
            var Q0;
            Q0=makeQuery(id+"F2.imprint","IMPRINT",FACE,{"disambiguationData":[TD([[makeQuery(id+"F2.imprint","IMPRINT",EDGE,{"derivedFrom":sQuery(id+"F2.wireOp",EDGE,"E180.MirrorCS")}),-1.0]])]});
            var Q1;
            Q1=makeQuery(id+"F2.imprint","IMPRINT",FACE,{"disambiguationData":[TD([[makeQuery(id+"F2.imprint","IMPRINT",EDGE,{"derivedFrom":sQuery(id+"F2.wireOp",EDGE,"E144.MirrorC")}),-1.0]])]});
            var Q2;
            Q2=makeQuery(id+"F2.imprint","IMPRINT",FACE,{"disambiguationData":[TD([[makeQuery(id+"F2.imprint","IMPRINT",EDGE,{"derivedFrom":sQuery(id+"F2.wireOp",EDGE,"E161")}),-1.0]])]});
            var Q3;
            {var subQ1=sQuery(id+"F2.wireOp",EDGE,"E209.MirrorCS");Q3=makeQuery(id+"F2.imprint","IMPRINT",FACE,{"disambiguationData":[TD([[makeQuery(id+"F2.imprint","IMPRINT",EDGE,{"derivedFrom":subQ1}),1.0]])]});}
            var Q4;
            Q4=makeQuery(id+"F2.imprint","IMPRINT",FACE,{"disambiguationData":[TD([[makeQuery(id+"F2.imprint","IMPRINT",EDGE,{"derivedFrom":sQuery(id+"F2.wireOp",EDGE,"E191.MirrorCS")}),1.0]])]});
            var Q5;
            Q5=makeQuery(id+"F2.imprint","IMPRINT",FACE,{"disambiguationData":[TD([[makeQuery(id+"F2.imprint","IMPRINT",EDGE,{"derivedFrom":sQuery(id+"F2.wireOp",EDGE,"E142")}),-1.0]])]});
            var Q6;
            {var subQ0=sQuery(id+"F2.wireOp",EDGE,"E288");Q6=makeQuery(id+"F2.imprint","IMPRINT",FACE,{"disambiguationData":[TD([[makeQuery(id+"F2.imprint","IMPRINT",EDGE,{"derivedFrom":subQ0}),1.0]])]});}
            var Q7;
            {var subQ0=sQuery(id+"F2.wireOp",EDGE,"E290.MirrorCS");Q7=makeQuery(id+"F2.imprint","IMPRINT",FACE,{"disambiguationData":[TD([[makeQuery(id+"F2.imprint","IMPRINT",EDGE,{"derivedFrom":subQ0}),-1.0]])]});}
            var Q8;
            Q8=makeQuery(id+"F2.imprint","IMPRINT",FACE,{"disambiguationData":[TD([[makeQuery(id+"F2.imprint","IMPRINT",EDGE,{"derivedFrom":sQuery(id+"F2.wireOp",EDGE,"E155")}),-1.0]])]});
            extrude(context, id + "F3", {"entities" : qUnion([Q0, Q1, Q2, Q3, Q4, Q5, Q6, Q7, Q8]), "depth" : 4 * mm});
        }
        {
            var Q0;
            Q0=makeQuery(id+"F2.imprint","IMPRINT",FACE,{"disambiguationData":[TD([[makeQuery(id+"F2.imprint","IMPRINT",EDGE,{"derivedFrom":sQuery(id+"F2.wireOp",EDGE,"E144.MirrorC")}),-1.0]])]});
            var Q1;
            Q1=makeQuery(id+"F2.imprint","IMPRINT",FACE,{"disambiguationData":[TD([[makeQuery(id+"F2.imprint","IMPRINT",EDGE,{"derivedFrom":sQuery(id+"F2.wireOp",EDGE,"E267")}),-1.0]])]});
            var Q2;
            Q2=makeQuery(id+"F2.imprint","IMPRINT",FACE,{"disambiguationData":[TD([[makeQuery(id+"F2.imprint","IMPRINT",EDGE,{"derivedFrom":sQuery(id+"F2.wireOp",EDGE,"E142")}),-1.0]])]});
            extrude(context, id + "F4", {"entities" : qUnion([Q0, Q1, Q2]), "oppositeDirection" : true, "depth" : 3 * mm});
        }
        {
            var Q0;
            Q0=makeQuery(id+"F4.opExtrude","SWEPT_BODY",BODY,{"disambiguationData":[OSD([sQuery(id+"F2.wireOp",EDGE,"E142"),sQuery(id+"F2.wireOp",EDGE,"E143.MirrorC"),sQuery(id+"F2.wireOp",EDGE,"E144.MirrorC"),sQuery(id+"F2.wireOp",EDGE,"E145.MirrorC"),sQuery(id+"F2.wireOp",EDGE,"E154"),sQuery(id+"F2.wireOp",EDGE,"E155"),sQuery(id+"F2.wireOp",EDGE,"E158"),sQuery(id+"F2.wireOp",EDGE,"E159"),sQuery(id+"F2.wireOp",EDGE,"E160"),sQuery(id+"F2.wireOp",EDGE,"E265"),sQuery(id+"F2.wireOp",EDGE,"E266.MirrorCS"),sQuery(id+"F2.wireOp",EDGE,"E267"),sQuery(id+"F2.wireOp",EDGE,"E268.MirrorCS"),sQuery(id+"F2.wireOp",EDGE,"E274.MirrorCS"),sQuery(id+"F2.wireOp",EDGE,"E275.MirrorCS"),sQuery(id+"F2.wireOp",EDGE,"E276"),sQuery(id+"F2.wireOp",EDGE,"E278"),sQuery(id+"F2.wireOp",EDGE,"E284"),sQuery(id+"F2.wireOp",EDGE,"E286.MirrorCS"),sQuery(id+"F2.wireOp",EDGE,"E288"),sQuery(id+"F2.wireOp",EDGE,"E289"),sQuery(id+"F2.wireOp",EDGE,"E290.MirrorCS"),sQuery(id+"F2.wireOp",EDGE,"E291.MirrorCS")])]});
            transform(context, id + "F5", {"entities" : qUnion([Q0]), "transformType" : TransformType.TRANSLATION_3D, "dx" : 0 * mm, "dy" : 0 * mm, "dz" : 7 * mm, "makeCopy" : true});
        }
        {
            var Q0;
            Q0=makeQuery(id+"F5.opPattern","COPY",BODY,{"derivedFrom":makeQuery(id+"F4.opExtrude","SWEPT_BODY",BODY,{"disambiguationData":[OSD([sQuery(id+"F2.wireOp",EDGE,"E142"),sQuery(id+"F2.wireOp",EDGE,"E143.MirrorC"),sQuery(id+"F2.wireOp",EDGE,"E144.MirrorC"),sQuery(id+"F2.wireOp",EDGE,"E145.MirrorC"),sQuery(id+"F2.wireOp",EDGE,"E155"),sQuery(id+"F2.wireOp",EDGE,"E158"),sQuery(id+"F2.wireOp",EDGE,"E159"),sQuery(id+"F2.wireOp",EDGE,"E160"),sQuery(id+"F2.wireOp",EDGE,"E265"),sQuery(id+"F2.wireOp",EDGE,"E266.MirrorCS"),sQuery(id+"F2.wireOp",EDGE,"E267"),sQuery(id+"F2.wireOp",EDGE,"E268.MirrorCS"),sQuery(id+"F2.wireOp",EDGE,"E278"),sQuery(id+"F2.wireOp",EDGE,"E284"),sQuery(id+"F2.wireOp",EDGE,"E286.MirrorCS"),sQuery(id+"F2.wireOp",EDGE,"E287"),sQuery(id+"F2.wireOp",EDGE,"E288"),sQuery(id+"F2.wireOp",EDGE,"E289"),sQuery(id+"F2.wireOp",EDGE,"E290.MirrorCS"),sQuery(id+"F2.wireOp",EDGE,"E291.MirrorCS")])]}),"instanceName":"1"});
            deleteBodies(context, id + "F6", {"entities" : qUnion([Q0])});
        }
        {
            var Q0;
            Q0=makeQuery(id+"F2.imprint","IMPRINT",FACE,{"disambiguationData":[TD([[makeQuery(id+"F2.imprint","IMPRINT",EDGE,{"derivedFrom":sQuery(id+"F2.wireOp",EDGE,"E273")}),-1.0]])]});
            var Q1;
            Q1=makeQuery(id+"F2.imprint","IMPRINT",FACE,{"disambiguationData":[TD([[makeQuery(id+"F2.imprint","IMPRINT",EDGE,{"derivedFrom":sQuery(id+"F2.wireOp",EDGE,"E154")}),-1.0]])]});
            var Q2;
            Q2=makeQuery(id+"F2.imprint","IMPRINT",FACE,{"disambiguationData":[TD([[makeQuery(id+"F2.imprint","IMPRINT",EDGE,{"derivedFrom":sQuery(id+"F2.wireOp",EDGE,"E144.MirrorC")}),-1.0]])]});
            var Q3;
            Q3=makeQuery(id+"F2.imprint","IMPRINT",FACE,{"disambiguationData":[TD([[makeQuery(id+"F2.imprint","IMPRINT",EDGE,{"derivedFrom":sQuery(id+"F2.wireOp",EDGE,"E267")}),-1.0]])]});
            var Q4;
            Q4=makeQuery(id+"F2.imprint","IMPRINT",FACE,{"disambiguationData":[TD([[makeQuery(id+"F2.imprint","IMPRINT",EDGE,{"derivedFrom":sQuery(id+"F2.wireOp",EDGE,"E142")}),-1.0]])]});
            var Q5;
            Q5=makeQuery(id+"F2.imprint","IMPRINT",FACE,{"disambiguationData":[TD([[makeQuery(id+"F2.imprint","IMPRINT",EDGE,{"derivedFrom":sQuery(id+"F2.wireOp",EDGE,"E155")}),-1.0]])]});
            extrude(context, id + "F7", {"entities" : qUnion([Q0, Q1, Q2, Q3, Q4, Q5]), "depth" : 6 * mm});
        }
        {
            var Q0;
            Q0=makeQuery(id+"F7.opExtrude","CAP_FACE",FACE,{"disambiguationData":[OSD([sQuery(id+"F2.wireOp",EDGE,"E142"),sQuery(id+"F2.wireOp",EDGE,"E143.MirrorC"),sQuery(id+"F2.wireOp",EDGE,"E144.MirrorC"),sQuery(id+"F2.wireOp",EDGE,"E145.MirrorC"),sQuery(id+"F2.wireOp",EDGE,"E154"),sQuery(id+"F2.wireOp",EDGE,"E155"),sQuery(id+"F2.wireOp",EDGE,"E158"),sQuery(id+"F2.wireOp",EDGE,"E159"),sQuery(id+"F2.wireOp",EDGE,"E160"),sQuery(id+"F2.wireOp",EDGE,"E265"),sQuery(id+"F2.wireOp",EDGE,"E266.MirrorCS"),sQuery(id+"F2.wireOp",EDGE,"E267"),sQuery(id+"F2.wireOp",EDGE,"E268.MirrorCS"),sQuery(id+"F2.wireOp",EDGE,"E274.MirrorCS"),sQuery(id+"F2.wireOp",EDGE,"E275.MirrorCS"),sQuery(id+"F2.wireOp",EDGE,"E276"),sQuery(id+"F2.wireOp",EDGE,"E278"),sQuery(id+"F2.wireOp",EDGE,"E284"),sQuery(id+"F2.wireOp",EDGE,"E286.MirrorCS"),sQuery(id+"F2.wireOp",EDGE,"E288"),sQuery(id+"F2.wireOp",EDGE,"E289"),sQuery(id+"F2.wireOp",EDGE,"E290.MirrorCS"),sQuery(id+"F2.wireOp",EDGE,"E291.MirrorCS")])],"isStart":true});
            extrude(context, id + "F8", {"entities" : qUnion([Q0]), "operationType" : NewBodyOperationType.REMOVE, "oppositeDirection" : true, "depth" : 5 * mm});
        }
    });
